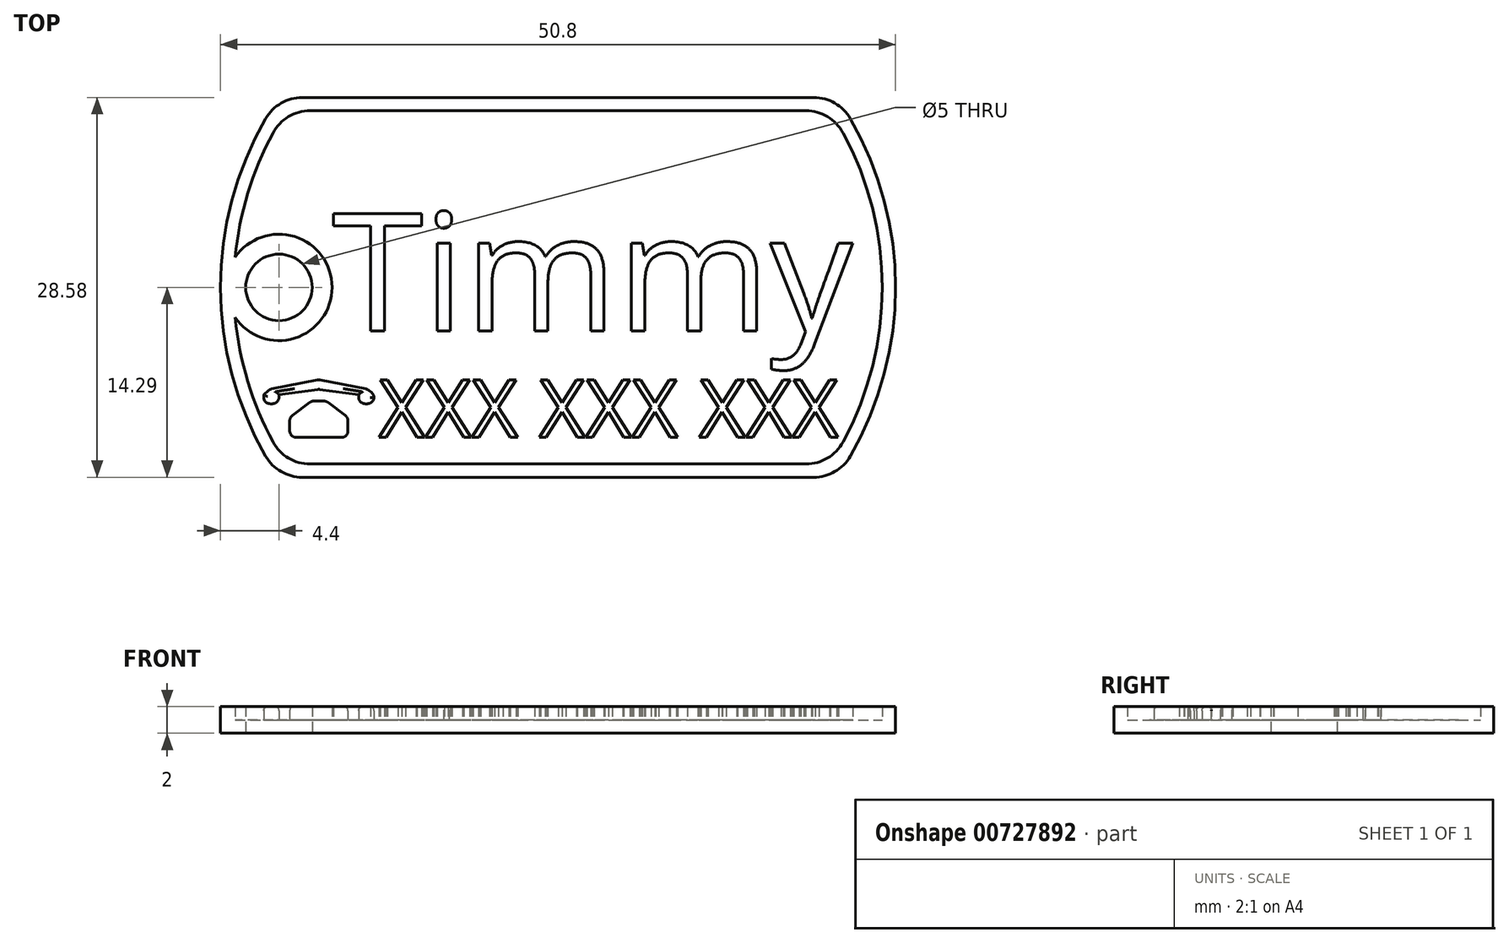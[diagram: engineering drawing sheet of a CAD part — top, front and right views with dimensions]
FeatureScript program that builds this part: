
annotation { "Feature Type Name" : "Feature", "Feature Type Description" : "" }
export const myFeature = defineFeature(function(context is Context, id is Id, definition is map)
    precondition{}
    {
        {
            var Q0;
            Q0=qCreatedBy(makeId("Top.planeOp"),FACE);
            var sketch = newSketch(context, id + "F0", { "sketchPlane" : qUnion([Q0])});
            skArc(sketch, "E0", {"start": v(-22, 12.7) * mm, "mid": v(-25.4, 0) * mm, "end": v(-22, -12.7) * mm});
            skLineSegment(sketch, "E1.top", {"start": v(-19.25, -14.29) * mm, "end": v(19.25, -14.29) * mm});
            skArc(sketch, "E2.trimOffspring", {"start": v(22, -12.7) * mm, "mid": v(25.4, 0) * mm, "end": v(22, 12.7) * mm});
            skLineSegment(sketch, "E3", {"start": v(-19.25, 14.29) * mm, "end": v(19.25, 14.29) * mm});
            skPoint(sketch, "E4.visualSharp", {"position": v(-21, 14.29) * mm});
            skArc(sketch, "E4.filletArc", {"start": v(-19.25, 14.29) * mm, "mid": v(-20.83, 13.86) * mm, "end": v(-22, 12.7) * mm});
            skPoint(sketch, "E5.visualSharp", {"position": v(21, 14.29) * mm});
            skArc(sketch, "E5.filletArc", {"start": v(22, 12.7) * mm, "mid": v(20.83, 13.86) * mm, "end": v(19.25, 14.29) * mm});
            skPoint(sketch, "E6.visualSharp", {"position": v(21, -14.29) * mm});
            skArc(sketch, "E6.filletArc", {"start": v(19.25, -14.29) * mm, "mid": v(20.83, -13.86) * mm, "end": v(22, -12.7) * mm});
            skPoint(sketch, "E7.visualSharp", {"position": v(-21, -14.29) * mm});
            skArc(sketch, "E7.filletArc", {"start": v(-22, -12.7) * mm, "mid": v(-20.83, -13.86) * mm, "end": v(-19.25, -14.29) * mm});
            skSolve(sketch);
        }
        {
            var Q0;
            Q0=makeQuery(id+"F0.imprint","IMPRINT",FACE,{"disambiguationData":[TD([[makeQuery(id+"F0.imprint","IMPRINT",EDGE,{"derivedFrom":sQuery(id+"F0.wireOp",EDGE,"E0")}),1.0]])]});
            extrude(context, id + "F1", {"entities" : qUnion([Q0]), "depth" : 1 * mm, "offsetDistance" : 25.4 * mm});
        }
        {
            var Q0;
            Q0=qCreatedBy(makeId("Top.planeOp"),FACE);
            var sketch = newSketch(context, id + "F2", { "sketchPlane" : qUnion([Q0])});
            skLineSegment(sketch, "E8.0", {"start": v(-18.66, 13.29) * mm, "end": v(18.66, 13.29) * mm});
            skArc(sketch, "E8.1", {"start": v(-21.45, 11.63) * mm, "mid": v(-24.4, 0) * mm, "end": v(-21.45, -11.63) * mm});
            skLineSegment(sketch, "E8.2", {"start": v(-18.66, -13.29) * mm, "end": v(18.66, -13.29) * mm});
            skArc(sketch, "E8.3", {"start": v(21.45, -11.63) * mm, "mid": v(24.4, 0) * mm, "end": v(21.45, 11.63) * mm});
            skPoint(sketch, "E9.visualSharp", {"position": v(-20.46, 13.29) * mm});
            skArc(sketch, "E9.filletArc", {"start": v(-18.66, 13.29) * mm, "mid": v(-20.29, 12.84) * mm, "end": v(-21.45, 11.63) * mm});
            skPoint(sketch, "E10.visualSharp", {"position": v(20.46, 13.29) * mm});
            skArc(sketch, "E10.filletArc", {"start": v(21.45, 11.63) * mm, "mid": v(20.29, 12.84) * mm, "end": v(18.66, 13.29) * mm});
            skPoint(sketch, "E11.visualSharp", {"position": v(20.46, -13.29) * mm});
            skArc(sketch, "E11.filletArc", {"start": v(18.66, -13.29) * mm, "mid": v(20.29, -12.84) * mm, "end": v(21.45, -11.63) * mm});
            skPoint(sketch, "E12.visualSharp", {"position": v(-20.46, -13.29) * mm});
            skArc(sketch, "E12.filletArc", {"start": v(-21.45, -11.63) * mm, "mid": v(-20.29, -12.84) * mm, "end": v(-18.66, -13.29) * mm});
            skLineSegment(sketch, "E13.0", {"start": v(-19.25, 14.29) * mm, "end": v(19.25, 14.29) * mm});
            skArc(sketch, "E13.1", {"start": v(-22, 12.7) * mm, "mid": v(-25.4, 0) * mm, "end": v(-22, -12.7) * mm});
            skLineSegment(sketch, "E13.2", {"start": v(-19.25, -14.29) * mm, "end": v(19.25, -14.29) * mm});
            skArc(sketch, "E13.3", {"start": v(22, -12.7) * mm, "mid": v(25.4, 0) * mm, "end": v(22, 12.7) * mm});
            skPoint(sketch, "E14.visualSharp", {"position": v(-21, -14.29) * mm});
            skArc(sketch, "E14.filletArc", {"start": v(-22, -12.7) * mm, "mid": v(-20.83, -13.86) * mm, "end": v(-19.25, -14.29) * mm});
            skPoint(sketch, "E15.visualSharp", {"position": v(21, -14.29) * mm});
            skArc(sketch, "E15.filletArc", {"start": v(19.25, -14.29) * mm, "mid": v(20.83, -13.86) * mm, "end": v(22, -12.7) * mm});
            skPoint(sketch, "E16.visualSharp", {"position": v(21, 14.29) * mm});
            skArc(sketch, "E16.filletArc", {"start": v(22, 12.7) * mm, "mid": v(20.83, 13.86) * mm, "end": v(19.25, 14.29) * mm});
            skPoint(sketch, "E17.visualSharp", {"position": v(-21, 14.29) * mm});
            skArc(sketch, "E17.filletArc", {"start": v(-19.25, 14.29) * mm, "mid": v(-20.83, 13.86) * mm, "end": v(-22, 12.7) * mm});
            skSolve(sketch);
        }
        {
            var Q0;
            Q0=makeQuery(id+"F2.imprint","IMPRINT",FACE,{"disambiguationData":[TD([[makeQuery(id+"F2.imprint","IMPRINT",EDGE,{"derivedFrom":sQuery(id+"F2.wireOp",EDGE,"E8.0")}),1.0]])]});
            extrude(context, id + "F3", {"entities" : qUnion([Q0]), "operationType" : NewBodyOperationType.ADD, "depth" : 2 * mm, "offsetDistance" : 25.4 * mm});
        }
        {
            var Q0;
            Q0=qCreatedBy(makeId("Top.planeOp"),FACE);
            var sketch = newSketch(context, id + "F4", { "sketchPlane" : qUnion([Q0])});
            skCircle(sketch, "E18", {"center": v(-21, 0) * mm, "radius": 2.5 * mm});
            skCircle(sketch, "E19", {"center": v(-21, 0) * mm, "radius": 4 * mm});
            skSolve(sketch);
        }
        {
            var Q0;
            Q0 = qSketchRegion(id + "F4", true);
            extrude(context, id + "F5", {"entities" : qUnion([Q0]), "operationType" : NewBodyOperationType.ADD, "depth" : 2 * mm, "offsetDistance" : 25 * mm});
        }
        {
            var Q0;
            Q0=qCreatedBy(makeId("Top.planeOp"),FACE);
            var sketch = newSketch(context, id + "F6", { "sketchPlane" : qUnion([Q0])});
            skCircle(sketch, "E20", {"center": v(-21, 0) * mm, "radius": 2.5 * mm});
            skSolve(sketch);
        }
        {
            var Q0;
            Q0 = qSketchRegion(id + "F6", true);
            extrude(context, id + "F7", {"entities" : qUnion([Q0]), "operationType" : NewBodyOperationType.REMOVE, "depth" : 5 * mm, "offsetDistance" : 25 * mm});
        }
        {
            var Q0;
            Q0=qCreatedBy(makeId("Top.planeOp"),FACE);
            var sketch = newSketch(context, id + "F8", { "sketchPlane" : qUnion([Q0])});
            skText(sketch, "E21", { "text": "Timmy", "fontName": "OpenSans-Regular.ttf"});
            const initialGuessF8  = {"E21": [-0.017, -0.00329, 1, 0, 0.0089]};
            skSetInitialGuess(sketch, initialGuessF8);
            skSolve(sketch);
        }
        {
            var Q0;
            Q0=qSketchRegion(id+"F8",true);
            extrude(context, id + "F9", {"entities" : qUnion([Q0]), "operationType" : NewBodyOperationType.ADD, "depth" : 2 * mm, "offsetDistance" : 25.4 * mm});
        }
        {
            var Q0;
            Q0=makeQuery(id+"F5.boolean.opBoolean","SPLIT",FACE,{"disambiguationData":[TD([makeQuery(id+"F3.opExtrude","SWEPT_FACE",FACE,{"disambiguationData":[OSD([sQuery(id+"F2.wireOp",EDGE,"E8.0")])]})])],"derivedFrom":makeQuery(id+"F1.opExtrude","CAP_FACE",FACE,{"disambiguationData":[OSD([sQuery(id+"F0.wireOp",EDGE,"E0"),sQuery(id+"F0.wireOp",EDGE,"E1.top"),sQuery(id+"F0.wireOp",EDGE,"E2.trimOffspring"),sQuery(id+"F0.wireOp",EDGE,"E3"),sQuery(id+"F0.wireOp",EDGE,"E4.filletArc"),sQuery(id+"F0.wireOp",EDGE,"E5.filletArc"),sQuery(id+"F0.wireOp",EDGE,"E6.filletArc"),sQuery(id+"F0.wireOp",EDGE,"E7.filletArc")])],"isStart":false})});
            var sketch = newSketch(context, id + "F10", { "sketchPlane" : qUnion([Q0])});
            skLineSegment(sketch, "E22", {"start": v(-18, -6.95) * mm, "end": v(-18, -12.21) * mm, "construction": true});
            skLineSegment(sketch, "E23", {"start": v(-18, -6.95) * mm, "end": v(-14.32, -7.67) * mm});
            skLineSegment(sketch, "E24", {"start": v(-14.32, -7.67) * mm, "end": v(-13.85, -8.08) * mm});
            skLineSegment(sketch, "E25", {"start": v(-13.85, -8.08) * mm, "end": v(-13.85, -8.76) * mm});
            skLineSegment(sketch, "E26", {"start": v(-13.85, -8.76) * mm, "end": v(-15, -8.76) * mm});
            skLineSegment(sketch, "E27", {"start": v(-15, -8.76) * mm, "end": v(-15, -8.08) * mm});
            skLineSegment(sketch, "E28", {"start": v(-15, -8.08) * mm, "end": v(-18, -7.67) * mm});
            skLineSegment(sketch, "E29", {"start": v(-18.54, -8.55) * mm, "end": v(-18, -8.55) * mm});
            skLineSegment(sketch, "E30", {"start": v(-18.54, -8.55) * mm, "end": v(-20.19, -9.8) * mm});
            skLineSegment(sketch, "E31", {"start": v(-20.19, -9.8) * mm, "end": v(-20.19, -11.29) * mm});
            skLineSegment(sketch, "E32", {"start": v(-18, -11.29) * mm, "end": v(-20.19, -11.29) * mm});
            skLineSegment(sketch, "E33.MirrorCS", {"start": v(-18, -6.95) * mm, "end": v(-21.68, -7.67) * mm});
            skLineSegment(sketch, "E34.MirrorCS", {"start": v(-21.68, -7.67) * mm, "end": v(-22.15, -8.08) * mm});
            skLineSegment(sketch, "E35.MirrorCS", {"start": v(-22.15, -8.08) * mm, "end": v(-22.15, -8.76) * mm});
            skLineSegment(sketch, "E36.MirrorCS", {"start": v(-22.15, -8.76) * mm, "end": v(-21, -8.76) * mm});
            skLineSegment(sketch, "E37.MirrorCS", {"start": v(-21, -8.76) * mm, "end": v(-21, -8.08) * mm});
            skLineSegment(sketch, "E38.MirrorCS", {"start": v(-21, -8.08) * mm, "end": v(-18, -7.67) * mm});
            skLineSegment(sketch, "E39.MirrorCS", {"start": v(-17.46, -8.55) * mm, "end": v(-18, -8.55) * mm});
            skLineSegment(sketch, "E40.MirrorCS", {"start": v(-17.46, -8.55) * mm, "end": v(-15.81, -9.8) * mm});
            skLineSegment(sketch, "E41.MirrorCS", {"start": v(-15.81, -9.8) * mm, "end": v(-15.81, -11.29) * mm});
            skLineSegment(sketch, "E42.MirrorCS", {"start": v(-18, -11.29) * mm, "end": v(-15.81, -11.29) * mm});
            skLineSegment(sketch, "E43", {"start": v(-20.8, -11.29) * mm, "end": v(-14.28, -11.29) * mm, "construction": true});
            skLineSegment(sketch, "E44", {"start": v(0, -15.2) * mm, "end": v(0, 0.7) * mm, "construction": true});
            skSolve(sketch);
        }
        {
            var Q0;
            Q0 = qSketchRegion(id + "F10", true);
            extrude(context, id + "F11", {"entities" : qUnion([Q0]), "operationType" : NewBodyOperationType.ADD, "depth" : 1 * mm, "offsetDistance" : 25 * mm});
        }
        {
            var Q0;
            Q0=makeQuery(id+"F11.opExtrude","SWEPT_EDGE",EDGE,{"disambiguationData":[OSD([sQuery(id+"F10.wireOp",EDGE,"E39.MirrorCS"),sQuery(id+"F10.wireOp",EDGE,"E40.MirrorCS")])]});
            var Q1;
            Q1=makeQuery(id+"F11.opExtrude","SWEPT_EDGE",EDGE,{"disambiguationData":[OSD([sQuery(id+"F10.wireOp",EDGE,"E29"),sQuery(id+"F10.wireOp",EDGE,"E30")])]});
            var Q2;
            Q2=makeQuery(id+"F11.opExtrude","SWEPT_EDGE",EDGE,{"disambiguationData":[OSD([sQuery(id+"F10.wireOp",EDGE,"E40.MirrorCS"),sQuery(id+"F10.wireOp",EDGE,"E41.MirrorCS")])]});
            var Q3;
            Q3=makeQuery(id+"F11.opExtrude","SWEPT_EDGE",EDGE,{"disambiguationData":[OSD([sQuery(id+"F10.wireOp",EDGE,"E41.MirrorCS"),sQuery(id+"F10.wireOp",EDGE,"E42.MirrorCS")])]});
            var Q4;
            Q4=makeQuery(id+"F11.opExtrude","SWEPT_EDGE",EDGE,{"disambiguationData":[OSD([sQuery(id+"F10.wireOp",EDGE,"E30"),sQuery(id+"F10.wireOp",EDGE,"E31")])]});
            var Q5;
            Q5=makeQuery(id+"F11.opExtrude","SWEPT_EDGE",EDGE,{"disambiguationData":[OSD([sQuery(id+"F10.wireOp",EDGE,"E31"),sQuery(id+"F10.wireOp",EDGE,"E32")])]});
            var Q6;
            Q6=makeQuery(id+"F11.opExtrude","SWEPT_EDGE",EDGE,{"disambiguationData":[OSD([sQuery(id+"F10.wireOp",EDGE,"E26"),sQuery(id+"F10.wireOp",EDGE,"E27")])]});
            var Q7;
            Q7=makeQuery(id+"F11.opExtrude","SWEPT_EDGE",EDGE,{"disambiguationData":[OSD([sQuery(id+"F10.wireOp",EDGE,"E36.MirrorCS"),sQuery(id+"F10.wireOp",EDGE,"E37.MirrorCS")])]});
            var Q8;
            Q8=makeQuery(id+"F11.opExtrude","SWEPT_EDGE",EDGE,{"disambiguationData":[OSD([sQuery(id+"F10.wireOp",EDGE,"E35.MirrorCS"),sQuery(id+"F10.wireOp",EDGE,"E36.MirrorCS")])]});
            fillet(context, id + "F12", {"entities" : qUnion([Q0, Q1, Q2, Q3, Q4, Q5, Q6, Q7, Q8]), "radius" : 0.5 * mm, "tangentPropagation" : true, "allowEdgeOverflow" : false});
        }
        {
            var Q0;
            Q0=makeQuery(id+"F11.opExtrude","SWEPT_EDGE",EDGE,{"disambiguationData":[OSD([sQuery(id+"F10.wireOp",EDGE,"E23"),sQuery(id+"F10.wireOp",EDGE,"E33.MirrorCS")])]});
            var Q1;
            Q1=makeQuery(id+"F11.opExtrude","SWEPT_EDGE",EDGE,{"disambiguationData":[OSD([sQuery(id+"F10.wireOp",EDGE,"E33.MirrorCS"),sQuery(id+"F10.wireOp",EDGE,"E34.MirrorCS")])]});
            var Q2;
            Q2=makeQuery(id+"F11.opExtrude","SWEPT_EDGE",EDGE,{"disambiguationData":[OSD([sQuery(id+"F10.wireOp",EDGE,"E23"),sQuery(id+"F10.wireOp",EDGE,"E24")])]});
            var Q3;
            Q3=makeQuery(id+"F12.opFillet","BLEND_EDGE",EDGE,{"blendedFrom":[makeQuery(id+"F11.opExtrude","SWEPT_EDGE",EDGE,{"disambiguationData":[OSD([sQuery(id+"F10.wireOp",EDGE,"E35.MirrorCS"),sQuery(id+"F10.wireOp",EDGE,"E36.MirrorCS")])]}),makeQuery(id+"F11.opExtrude","SWEPT_FACE",FACE,{"disambiguationData":[OSD([sQuery(id+"F10.wireOp",EDGE,"E34.MirrorCS")])]})],"blendedInto":[makeQuery(id+"F11.opExtrude","SWEPT_FACE",FACE,{"disambiguationData":[OSD([sQuery(id+"F10.wireOp",EDGE,"E34.MirrorCS")])]})]});
            var Q4;
            Q4=makeQuery(id+"F11.opExtrude","SWEPT_EDGE",EDGE,{"disambiguationData":[OSD([sQuery(id+"F10.wireOp",EDGE,"E24"),sQuery(id+"F10.wireOp",EDGE,"E25")])]});
            var Q5;
            Q5=makeQuery(id+"F11.opExtrude","SWEPT_EDGE",EDGE,{"disambiguationData":[OSD([sQuery(id+"F10.wireOp",EDGE,"E25"),sQuery(id+"F10.wireOp",EDGE,"E26")])]});
            var Q6;
            Q6=makeQuery(id+"F12.opFillet","BLEND_EDGE",EDGE,{"blendedFrom":[makeQuery(id+"F11.opExtrude","SWEPT_EDGE",EDGE,{"disambiguationData":[OSD([sQuery(id+"F10.wireOp",EDGE,"E26"),sQuery(id+"F10.wireOp",EDGE,"E27")])]}),makeQuery(id+"F11.opExtrude","SWEPT_FACE",FACE,{"disambiguationData":[OSD([sQuery(id+"F10.wireOp",EDGE,"E28")])]})],"blendedInto":[makeQuery(id+"F11.opExtrude","SWEPT_FACE",FACE,{"disambiguationData":[OSD([sQuery(id+"F10.wireOp",EDGE,"E28")])]})]});
            var Q7;
            Q7=makeQuery(id+"F11.opExtrude","SWEPT_EDGE",EDGE,{"disambiguationData":[OSD([sQuery(id+"F10.wireOp",EDGE,"E28"),sQuery(id+"F10.wireOp",EDGE,"E38.MirrorCS")])]});
            var Q8;
            Q8=makeQuery(id+"F12.opFillet","BLEND_EDGE",EDGE,{"blendedFrom":[makeQuery(id+"F11.opExtrude","SWEPT_EDGE",EDGE,{"disambiguationData":[OSD([sQuery(id+"F10.wireOp",EDGE,"E36.MirrorCS"),sQuery(id+"F10.wireOp",EDGE,"E37.MirrorCS")])]}),makeQuery(id+"F11.opExtrude","SWEPT_FACE",FACE,{"disambiguationData":[OSD([sQuery(id+"F10.wireOp",EDGE,"E38.MirrorCS")])]})],"blendedInto":[makeQuery(id+"F11.opExtrude","SWEPT_FACE",FACE,{"disambiguationData":[OSD([sQuery(id+"F10.wireOp",EDGE,"E38.MirrorCS")])]})]});
            fillet(context, id + "F13", {"entities" : qUnion([Q0, Q1, Q2, Q3, Q4, Q5, Q6, Q7, Q8]), "radius" : 0.5 * mm, "tangentPropagation" : true, "allowEdgeOverflow" : false});
        }
        {
            var Q0;
            Q0=makeQuery(id+"F11.opExtrude","CAP_EDGE",EDGE,{"disambiguationData":[OSD([sQuery(id+"F10.wireOp",EDGE,"E33.MirrorCS")])],"isStart":false});
            var Q1;
            Q1=makeQuery(id+"F11.opExtrude","CAP_EDGE",EDGE,{"disambiguationData":[OSD([sQuery(id+"F10.wireOp",EDGE,"E38.MirrorCS")])],"isStart":false});
            var Q2;
            {var subQ0=sQuery(id+"F10.wireOp",EDGE,"E27");var subQ1=sQuery(id+"F10.wireOp",EDGE,"E26");Q2=makeQuery(id+"F12.opFillet","BLEND_EDGE",EDGE,{"blendedFrom":[makeQuery(id+"F11.opExtrude","SWEPT_EDGE",EDGE,{"disambiguationData":[OSD([subQ1,subQ0])]}),makeQuery(id+"F11.opExtrude","CAP_FACE",FACE,{"disambiguationData":[OSD([sQuery(id+"F10.wireOp",EDGE,"E23"),sQuery(id+"F10.wireOp",EDGE,"E24"),sQuery(id+"F10.wireOp",EDGE,"E25"),subQ1,subQ0,sQuery(id+"F10.wireOp",EDGE,"E28"),sQuery(id+"F10.wireOp",EDGE,"E33.MirrorCS"),sQuery(id+"F10.wireOp",EDGE,"E34.MirrorCS"),sQuery(id+"F10.wireOp",EDGE,"E35.MirrorCS"),sQuery(id+"F10.wireOp",EDGE,"E36.MirrorCS"),sQuery(id+"F10.wireOp",EDGE,"E37.MirrorCS"),sQuery(id+"F10.wireOp",EDGE,"E38.MirrorCS")])],"isStart":false})],"blendedInto":[makeQuery(id+"F11.opExtrude","CAP_FACE",FACE,{"disambiguationData":[OSD([sQuery(id+"F10.wireOp",EDGE,"E23"),sQuery(id+"F10.wireOp",EDGE,"E24"),sQuery(id+"F10.wireOp",EDGE,"E25"),subQ1,subQ0,sQuery(id+"F10.wireOp",EDGE,"E28"),sQuery(id+"F10.wireOp",EDGE,"E33.MirrorCS"),sQuery(id+"F10.wireOp",EDGE,"E34.MirrorCS"),sQuery(id+"F10.wireOp",EDGE,"E35.MirrorCS"),sQuery(id+"F10.wireOp",EDGE,"E36.MirrorCS"),sQuery(id+"F10.wireOp",EDGE,"E37.MirrorCS"),sQuery(id+"F10.wireOp",EDGE,"E38.MirrorCS")])],"isStart":false})]});}
            var Q3;
            {var subQ0=sQuery(id+"F10.wireOp",EDGE,"E37.MirrorCS");var subQ1=sQuery(id+"F10.wireOp",EDGE,"E36.MirrorCS");Q3=makeQuery(id+"F12.opFillet","BLEND_EDGE",EDGE,{"blendedFrom":[makeQuery(id+"F11.opExtrude","SWEPT_EDGE",EDGE,{"disambiguationData":[OSD([subQ1,subQ0])]}),makeQuery(id+"F11.opExtrude","CAP_FACE",FACE,{"disambiguationData":[OSD([sQuery(id+"F10.wireOp",EDGE,"E23"),sQuery(id+"F10.wireOp",EDGE,"E24"),sQuery(id+"F10.wireOp",EDGE,"E25"),sQuery(id+"F10.wireOp",EDGE,"E26"),sQuery(id+"F10.wireOp",EDGE,"E27"),sQuery(id+"F10.wireOp",EDGE,"E28"),sQuery(id+"F10.wireOp",EDGE,"E33.MirrorCS"),sQuery(id+"F10.wireOp",EDGE,"E34.MirrorCS"),sQuery(id+"F10.wireOp",EDGE,"E35.MirrorCS"),subQ1,subQ0,sQuery(id+"F10.wireOp",EDGE,"E38.MirrorCS")])],"isStart":false})],"blendedInto":[makeQuery(id+"F11.opExtrude","CAP_FACE",FACE,{"disambiguationData":[OSD([sQuery(id+"F10.wireOp",EDGE,"E23"),sQuery(id+"F10.wireOp",EDGE,"E24"),sQuery(id+"F10.wireOp",EDGE,"E25"),sQuery(id+"F10.wireOp",EDGE,"E26"),sQuery(id+"F10.wireOp",EDGE,"E27"),sQuery(id+"F10.wireOp",EDGE,"E28"),sQuery(id+"F10.wireOp",EDGE,"E33.MirrorCS"),sQuery(id+"F10.wireOp",EDGE,"E34.MirrorCS"),sQuery(id+"F10.wireOp",EDGE,"E35.MirrorCS"),subQ1,subQ0,sQuery(id+"F10.wireOp",EDGE,"E38.MirrorCS")])],"isStart":false})]});}
            var Q4;
            Q4=makeQuery(id+"F11.opExtrude","CAP_EDGE",EDGE,{"disambiguationData":[OSD([sQuery(id+"F10.wireOp",EDGE,"E30")])],"isStart":false});
            fillet(context, id + "F14", {"entities" : qUnion([Q0, Q1, Q2, Q3, Q4]), "radius" : .3 * mm, "tangentPropagation" : true, "allowEdgeOverflow" : false});
        }
        {
            var Q0;
            Q0=makeQuery(id+"F10.imprint","IMPRINT",FACE,{"disambiguationData":[TD([[makeQuery(id+"F10.imprint","IMPRINT",EDGE,{"derivedFrom":sQuery(id+"F10.wireOp",EDGE,"E23")}),1.0]])]});
            var sketch = newSketch(context, id + "F15", { "sketchPlane" : qUnion([Q0])});
            skText(sketch, "E45", { "text": "XXX XXX XXX", "fontName": "OpenSans-Regular.ttf"});
            const initialGuessF15  = {"E45": [-0.0135, -0.01129, 1, 0, 0.00436]};
            skSetInitialGuess(sketch, initialGuessF15);
            skSolve(sketch);
        }
        {
            var Q0;
            Q0 = qSketchRegion(id + "F15", true);
            extrude(context, id + "F16", {"entities" : qUnion([Q0]), "operationType" : NewBodyOperationType.ADD, "depth" : 1 * mm, "offsetDistance" : 25 * mm});
        }
    });
